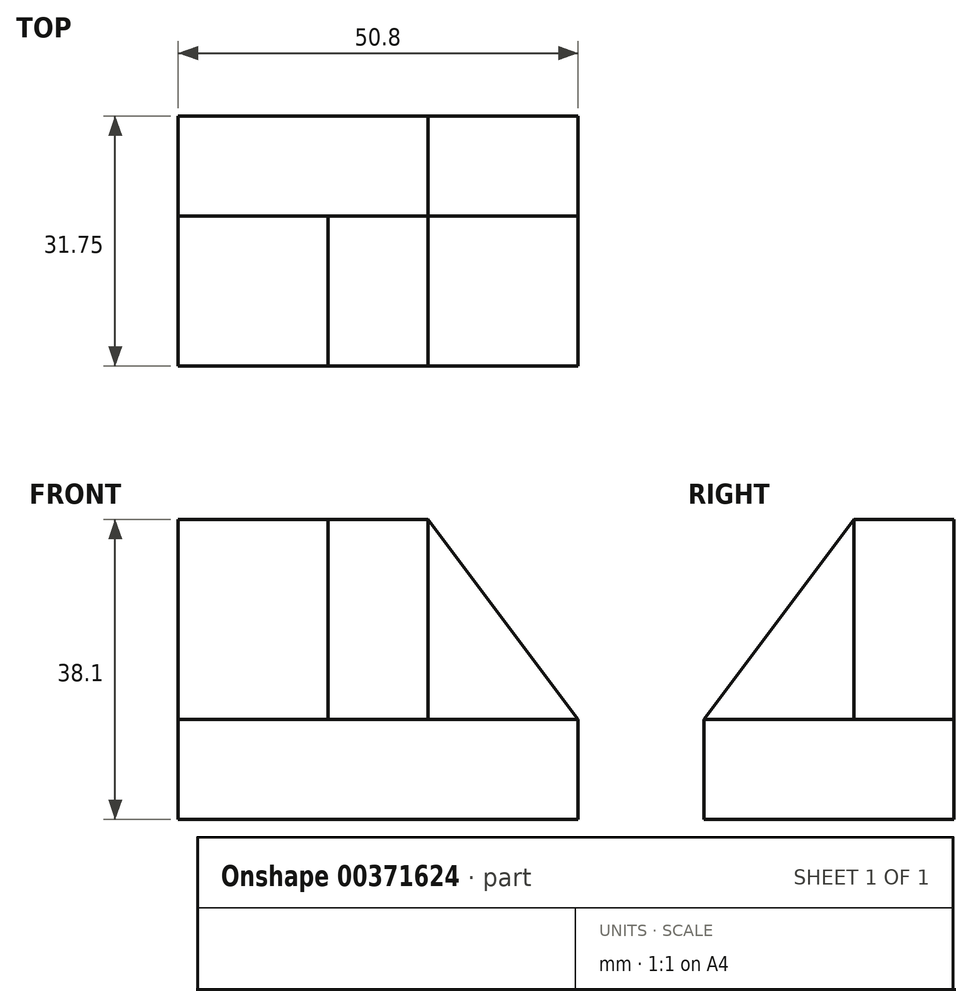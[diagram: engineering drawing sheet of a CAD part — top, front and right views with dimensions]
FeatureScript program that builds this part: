
annotation { "Feature Type Name" : "Feature", "Feature Type Description" : "" }
export const myFeature = defineFeature(function(context is Context, id is Id, definition is map)
    precondition{}
    {
        {
            var Q0;
            Q0=qCreatedBy(makeId("Front.planeOp"),FACE);
            var sketch = newSketch(context, id + "F0", { "sketchPlane" : qUnion([Q0])});
            skLineSegment(sketch, "E0", {"start": v(50.8, 0) * mm, "end": v(50.8, 38.1) * mm});
            skLineSegment(sketch, "E1", {"start": v(50.8, 38.1) * mm, "end": v(0, 38.1) * mm});
            skLineSegment(sketch, "E2", {"start": v(0, 38.1) * mm, "end": v(0, 0) * mm});
            skLineSegment(sketch, "E3", {"start": v(0, 0) * mm, "end": v(50.8, 0) * mm});
            skSolve(sketch);
        }
        {
            var Q0;
            Q0=makeQuery(id+"F0.imprint","IMPRINT",FACE,{"disambiguationData":[TD([[makeQuery(id+"F0.imprint","IMPRINT",EDGE,{"derivedFrom":sQuery(id+"F0.wireOp",EDGE,"E0")}),1.0]])]});
            extrude(context, id + "F1", {"entities" : qUnion([Q0]), "depth" : 31.75 * mm});
        }
        {
            var Q0;
            Q0=makeQuery(id+"F1.opExtrude","CAP_FACE",FACE,{"disambiguationData":[OSD([sQuery(id+"F0.wireOp",EDGE,"E0"),sQuery(id+"F0.wireOp",EDGE,"E1"),sQuery(id+"F0.wireOp",EDGE,"E2"),sQuery(id+"F0.wireOp",EDGE,"E3")])],"isStart":false});
            var sketch = newSketch(context, id + "F2", { "sketchPlane" : qUnion([Q0])});
            skLineSegment(sketch, "E4", {"start": v(31.75, 38.1) * mm, "end": v(50.8, 12.7) * mm});
            skSolve(sketch);
        }
        {
            var Q0;
            {var subQ0=sQuery(id+"F2.wireOp",EDGE,"E4");Q0=makeQuery(id+"F2.imprint","IMPRINT",FACE,{"disambiguationData":[TD([[makeQuery(id+"F2.imprint","IMPRINT",EDGE,{"derivedFrom":subQ0}),1.0]])]});}
            extrude(context, id + "F3", {"entities" : qUnion([Q0]), "operationType" : NewBodyOperationType.REMOVE, "oppositeDirection" : true, "depth" : 31.75 * mm});
        }
        {
            var Q0;
            Q0=makeQuery(id+"F1.opExtrude","CAP_FACE",FACE,{"disambiguationData":[OSD([sQuery(id+"F0.wireOp",EDGE,"E0"),sQuery(id+"F0.wireOp",EDGE,"E1"),sQuery(id+"F0.wireOp",EDGE,"E2"),sQuery(id+"F0.wireOp",EDGE,"E3")])],"isStart":false});
            var sketch = newSketch(context, id + "F4", { "sketchPlane" : qUnion([Q0])});
            skLineSegment(sketch, "E5", {"start": v(19.05, 38.1) * mm, "end": v(0, 12.7) * mm});
            skSolve(sketch);
        }
        {
            var Q0;
            {var subQ0=sQuery(id+"F4.wireOp",EDGE,"E5");Q0=makeQuery(id+"F4.imprint","IMPRINT",FACE,{"disambiguationData":[TD([[makeQuery(id+"F4.imprint","IMPRINT",EDGE,{"derivedFrom":subQ0}),-1.0]])]});}
            extrude(context, id + "F5", {"entities" : qUnion([Q0]), "operationType" : NewBodyOperationType.REMOVE, "oppositeDirection" : true, "depth" : 31.75 * mm});
        }
        {
            var Q0;
            Q0=makeQuery(id+"F1.opExtrude","CAP_FACE",FACE,{"disambiguationData":[OSD([sQuery(id+"F0.wireOp",EDGE,"E0"),sQuery(id+"F0.wireOp",EDGE,"E1"),sQuery(id+"F0.wireOp",EDGE,"E2"),sQuery(id+"F0.wireOp",EDGE,"E3")])],"isStart":false});
            var sketch = newSketch(context, id + "F6", { "sketchPlane" : qUnion([Q0])});
            skLineSegment(sketch, "E6", {"start": v(50.8, 12.7) * mm, "end": v(31.75, 12.7) * mm});
            skLineSegment(sketch, "E7", {"start": v(31.75, 12.7) * mm, "end": v(31.75, 38.1) * mm});
            skSolve(sketch);
        }
        {
            var Q0;
            Q0 = qSketchRegion(id + "F6", true);
            var Q1;
            Q1=makeQuery(id+"F6.imprint","IMPRINT",FACE,{"disambiguationData":[TD([[makeQuery(id+"F6.imprint","IMPRINT",EDGE,{"derivedFrom":sQuery(id+"F6.wireOp",EDGE,"E6")}),-1.0]])]});
            extrude(context, id + "F7", {"entities" : qUnion([Q0, Q1]), "operationType" : NewBodyOperationType.REMOVE, "oppositeDirection" : true, "depth" : 19.05 * mm});
        }
        {
            var Q0;
            Q0=makeQuery(id+"F1.opExtrude","CAP_FACE",FACE,{"disambiguationData":[OSD([sQuery(id+"F0.wireOp",EDGE,"E0"),sQuery(id+"F0.wireOp",EDGE,"E1"),sQuery(id+"F0.wireOp",EDGE,"E2"),sQuery(id+"F0.wireOp",EDGE,"E3")])],"isStart":false});
            var sketch = newSketch(context, id + "F8", { "sketchPlane" : qUnion([Q0])});
            skLineSegment(sketch, "E8", {"start": v(0, 12.7) * mm, "end": v(19.05, 12.7) * mm});
            skLineSegment(sketch, "E9", {"start": v(19.05, 12.7) * mm, "end": v(19.05, 38.1) * mm});
            skSolve(sketch);
        }
        {
            var Q0;
            Q0=makeQuery(id+"F8.imprint","IMPRINT",FACE,{"disambiguationData":[TD([[makeQuery(id+"F8.imprint","IMPRINT",EDGE,{"derivedFrom":sQuery(id+"F8.wireOp",EDGE,"E8")}),1.0]])]});
            extrude(context, id + "F9", {"entities" : qUnion([Q0]), "operationType" : NewBodyOperationType.REMOVE, "oppositeDirection" : true, "depth" : 19.05 * mm});
        }
        {
            var Q0;
            Q0=makeQuery(id+"F1.opExtrude","CAP_FACE",FACE,{"disambiguationData":[OSD([sQuery(id+"F0.wireOp",EDGE,"E0"),sQuery(id+"F0.wireOp",EDGE,"E1"),sQuery(id+"F0.wireOp",EDGE,"E2"),sQuery(id+"F0.wireOp",EDGE,"E3")])],"isStart":true});
            var sketch = newSketch(context, id + "F10", { "sketchPlane" : qUnion([Q0])});
            skLineSegment(sketch, "E10", {"start": v(-19.05, 38.1) * mm, "end": v(0, 38.1) * mm});
            skLineSegment(sketch, "E11", {"start": v(0, 38.1) * mm, "end": v(0, 12.7) * mm});
            skSolve(sketch);
        }
        {
            var Q0;
            Q0 = qSketchRegion(id + "F10", true);
            var Q1;
            Q1=makeQuery(id+"F10.imprint","IMPRINT",FACE,{"disambiguationData":[TD([[makeQuery(id+"F10.imprint","IMPRINT",EDGE,{"derivedFrom":sQuery(id+"F10.wireOp",EDGE,"E10")}),-1.0]])]});
            extrude(context, id + "F11", {"entities" : qUnion([Q0, Q1]), "operationType" : NewBodyOperationType.ADD, "oppositeDirection" : true, "depth" : 12.7 * mm});
        }
        {
            var Q0;
            Q0=makeQuery(id+"F9.boolean.opBoolean","COPY",FACE,{"derivedFrom":makeQuery(id+"F9.opExtrude","SWEPT_FACE",FACE,{"disambiguationData":[OSD([sQuery(id+"F8.wireOp",EDGE,"E9")])]})});
            var sketch = newSketch(context, id + "F12", { "sketchPlane" : qUnion([Q0])});
            skLineSegment(sketch, "E12", {"start": v(12.7, 38.1) * mm, "end": v(31.75, 12.7) * mm});
            skSolve(sketch);
        }
        {
            var Q0;
            Q0 = qSketchRegion(id + "F12", true);
            var Q1;
            Q1=makeQuery(id+"F12.imprint","IMPRINT",FACE,{"disambiguationData":[TD([[makeQuery(id+"F12.imprint","IMPRINT",EDGE,{"derivedFrom":sQuery(id+"F12.wireOp",EDGE,"E12")}),1.0]])]});
            extrude(context, id + "F13", {"entities" : qUnion([Q0, Q1]), "operationType" : NewBodyOperationType.REMOVE, "oppositeDirection" : true, "depth" : 12.7 * mm});
        }
    });
